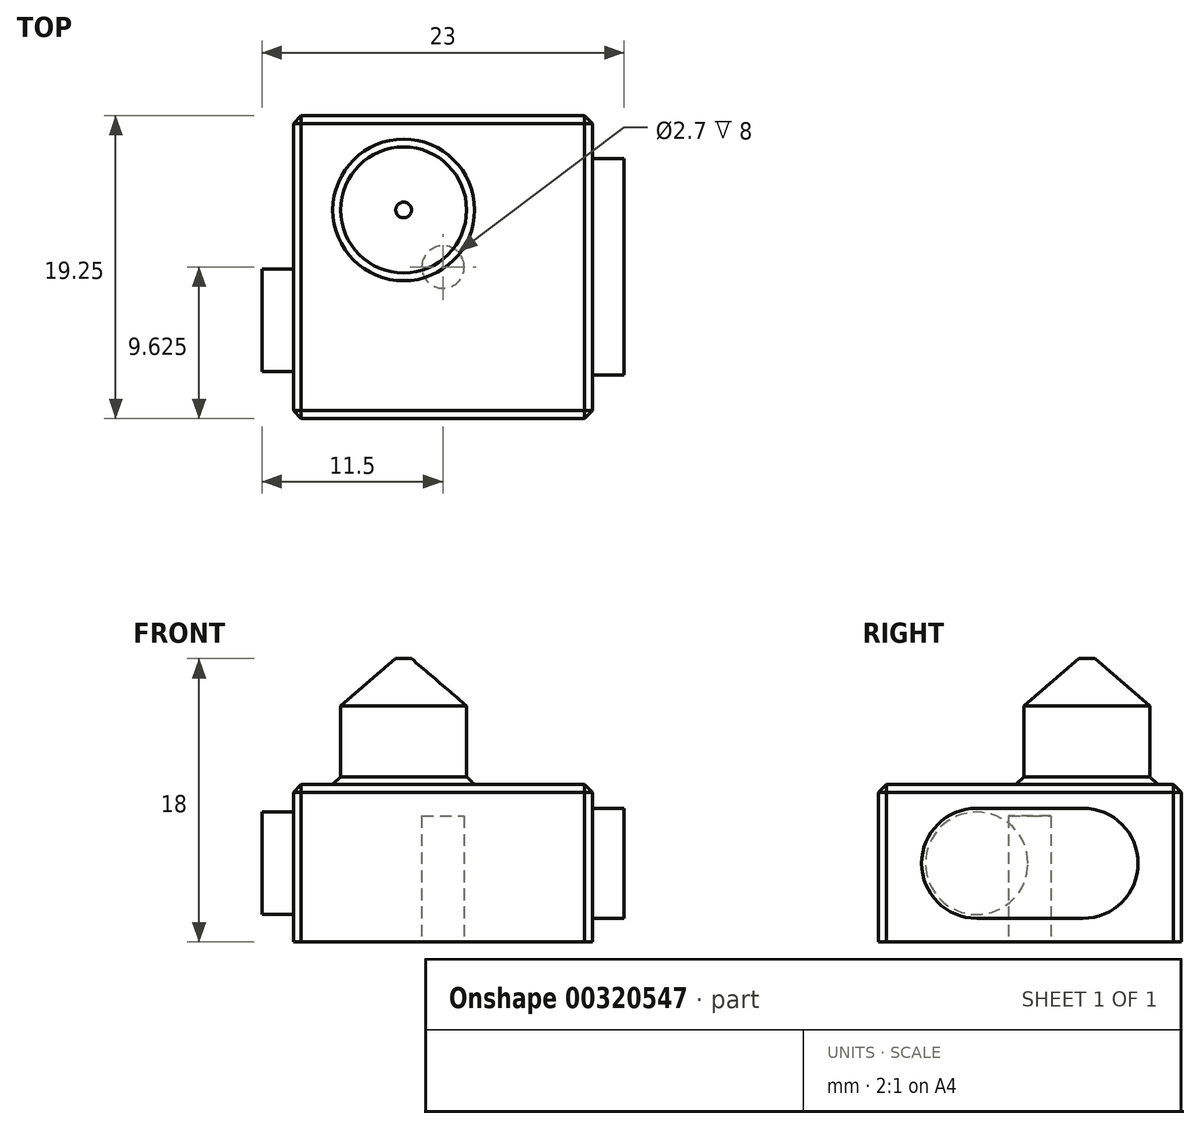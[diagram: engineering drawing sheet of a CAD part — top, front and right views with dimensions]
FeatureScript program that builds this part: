
annotation { "Feature Type Name" : "Feature", "Feature Type Description" : "" }
export const myFeature = defineFeature(function(context is Context, id is Id, definition is map)
    precondition{}
    {
        {
            var Q0;
            Q0=qCreatedBy(makeId("Top.planeOp"),FACE);
            var sketch = newSketch(context, id + "F0", { "sketchPlane" : qUnion([Q0])});
            skLineSegment(sketch, "E0.bottom", {"start": v(0, 0) * mm, "end": v(19, 0) * mm});
            skLineSegment(sketch, "E0.top", {"start": v(0, 19.25) * mm, "end": v(19, 19.25) * mm});
            skLineSegment(sketch, "E0.left", {"start": v(0, 0) * mm, "end": v(0, 19.25) * mm});
            skLineSegment(sketch, "E0.right", {"start": v(19, 0) * mm, "end": v(19, 19.25) * mm});
            skSolve(sketch);
        }
        {
            var Q0;
            Q0 = qSketchRegion(id + "F0", true);
            extrude(context, id + "F1", {"entities" : qUnion([Q0]), "depth" : 10 * mm});
        }
        {
            var Q0;
            Q0=makeQuery(id+"F1.opExtrude","CAP_FACE",FACE,{"disambiguationData":[OSD([sQuery(id+"F0.wireOp",EDGE,"E0.bottom"),sQuery(id+"F0.wireOp",EDGE,"E0.top"),sQuery(id+"F0.wireOp",EDGE,"E0.left"),sQuery(id+"F0.wireOp",EDGE,"E0.right")])],"isStart":false});
            var sketch = newSketch(context, id + "F2", { "sketchPlane" : qUnion([Q0])});
            skCircle(sketch, "E1", {"center": v(7, 13.25) * mm, "radius": 4 * mm});
            skSolve(sketch);
        }
        {
            var Q0;
            Q0 = qSketchRegion(id + "F2", true);
            extrude(context, id + "F3", {"entities" : qUnion([Q0]), "operationType" : NewBodyOperationType.ADD, "depth" : 8 * mm});
        }
        {
            var Q0;
            Q0=makeQuery(id+"F3.opExtrude","CAP_EDGE",EDGE,{"disambiguationData":[OSD([sQuery(id+"F2.wireOp",EDGE,"E1")])],"isStart":false});
            chamfer(context, id + "F4", {"entities" : qUnion([Q0]), "chamferType" : ChamferType.TWO_OFFSETS, "width1" : 3.5 * mm, "oppositeDirection" : false, "width2" : 3 * mm, "tangentPropagation" : true});
        }
        {
            var Q0;
            Q0=makeQuery(id+"F1.opExtrude","SWEPT_FACE",FACE,{"disambiguationData":[OSD([sQuery(id+"F0.wireOp",EDGE,"E0.left")])]});
            var sketch = newSketch(context, id + "F5", { "sketchPlane" : qUnion([Q0])});
            skLineSegment(sketch, "E2", {"start": v(-19.25, 5) * mm, "end": v(0, 5) * mm, "construction": true});
            skCircle(sketch, "E3", {"center": v(-6.25, 5) * mm, "radius": 3.25 * mm});
            skSolve(sketch);
        }
        {
            var Q0;
            Q0 = qSketchRegion(id + "F5", true);
            extrude(context, id + "F6", {"entities" : qUnion([Q0]), "operationType" : NewBodyOperationType.ADD, "depth" : 2 * mm});
        }
        {
            var Q0;
            Q0=makeQuery(id+"F1.opExtrude","SWEPT_FACE",FACE,{"disambiguationData":[OSD([sQuery(id+"F0.wireOp",EDGE,"E0.right")])]});
            var sketch = newSketch(context, id + "F7", { "sketchPlane" : qUnion([Q0])});
            skLineSegment(sketch, "E4", {"start": v(0, 5) * mm, "end": v(19.25, 5) * mm, "construction": true});
            skArc(sketch, "E5", {"start": v(6.25, 8.5) * mm, "mid": v(2.75, 5) * mm, "end": v(6.25, 1.5) * mm});
            skArc(sketch, "E6", {"start": v(13, 1.5) * mm, "mid": v(16.5, 5) * mm, "end": v(13, 8.5) * mm});
            skLineSegment(sketch, "E7", {"start": v(6.25, 8.5) * mm, "end": v(13, 8.5) * mm});
            skLineSegment(sketch, "E8", {"start": v(6.25, 1.5) * mm, "end": v(13, 1.5) * mm});
            skSolve(sketch);
        }
        {
            var Q0;
            Q0 = qSketchRegion(id + "F7", true);
            extrude(context, id + "F8", {"entities" : qUnion([Q0]), "operationType" : NewBodyOperationType.ADD, "depth" : 2 * mm});
        }
        {
            var Q0;
            Q0=makeQuery(id+"F1.opExtrude","SWEPT_EDGE",EDGE,{"disambiguationData":[OSD([sQuery(id+"F0.wireOp",EDGE,"E0.top"),sQuery(id+"F0.wireOp",EDGE,"E0.right")])]});
            var Q1;
            Q1=makeQuery(id+"F1.opExtrude","SWEPT_EDGE",EDGE,{"disambiguationData":[OSD([sQuery(id+"F0.wireOp",EDGE,"E0.top"),sQuery(id+"F0.wireOp",EDGE,"E0.left")])]});
            var Q2;
            Q2=makeQuery(id+"F1.opExtrude","SWEPT_EDGE",EDGE,{"disambiguationData":[OSD([sQuery(id+"F0.wireOp",EDGE,"E0.bottom"),sQuery(id+"F0.wireOp",EDGE,"E0.left")])]});
            var Q3;
            Q3=makeQuery(id+"F1.opExtrude","SWEPT_EDGE",EDGE,{"disambiguationData":[OSD([sQuery(id+"F0.wireOp",EDGE,"E0.bottom"),sQuery(id+"F0.wireOp",EDGE,"E0.right")])]});
            var Q4;
            Q4=makeQuery(id+"F1.opExtrude","CAP_FACE",FACE,{"disambiguationData":[OSD([sQuery(id+"F0.wireOp",EDGE,"E0.bottom"),sQuery(id+"F0.wireOp",EDGE,"E0.top"),sQuery(id+"F0.wireOp",EDGE,"E0.left"),sQuery(id+"F0.wireOp",EDGE,"E0.right")])],"isStart":false});
            var Q5;
            Q5=makeQuery(id+"F6.opExtrude","CAP_EDGE",EDGE,{"disambiguationData":[OSD([sQuery(id+"F5.wireOp",EDGE,"E3")])],"isStart":true});
            var Q6;
            Q6=makeQuery(id+"F8.opExtrude","CAP_EDGE",EDGE,{"disambiguationData":[OSD([sQuery(id+"F7.wireOp",EDGE,"E7")])],"isStart":true});
            chamfer(context, id + "F9", {"entities" : qUnion([Q0, Q1, Q2, Q3, Q4, Q5, Q6]), "width" : 0.5 * mm, "tangentPropagation" : true});
        }
        {
            var Q0;
            Q0=makeQuery(id+"F1.opExtrude","CAP_FACE",FACE,{"disambiguationData":[OSD([sQuery(id+"F0.wireOp",EDGE,"E0.bottom"),sQuery(id+"F0.wireOp",EDGE,"E0.top"),sQuery(id+"F0.wireOp",EDGE,"E0.left"),sQuery(id+"F0.wireOp",EDGE,"E0.right")])],"isStart":true});
            var sketch = newSketch(context, id + "F10", { "sketchPlane" : qUnion([Q0])});
            skLineSegment(sketch, "E9", {"start": v(9.5, 0) * mm, "end": v(9.5, -19.25) * mm, "construction": true});
            skCircle(sketch, "E10", {"center": v(9.5, -9.62) * mm, "radius": 1.35 * mm});
            skSolve(sketch);
        }
        {
            var Q0;
            Q0 = qSketchRegion(id + "F10", true);
            extrude(context, id + "F11", {"entities" : qUnion([Q0]), "operationType" : NewBodyOperationType.REMOVE, "oppositeDirection" : true, "depth" : 8 * mm});
        }
    });
